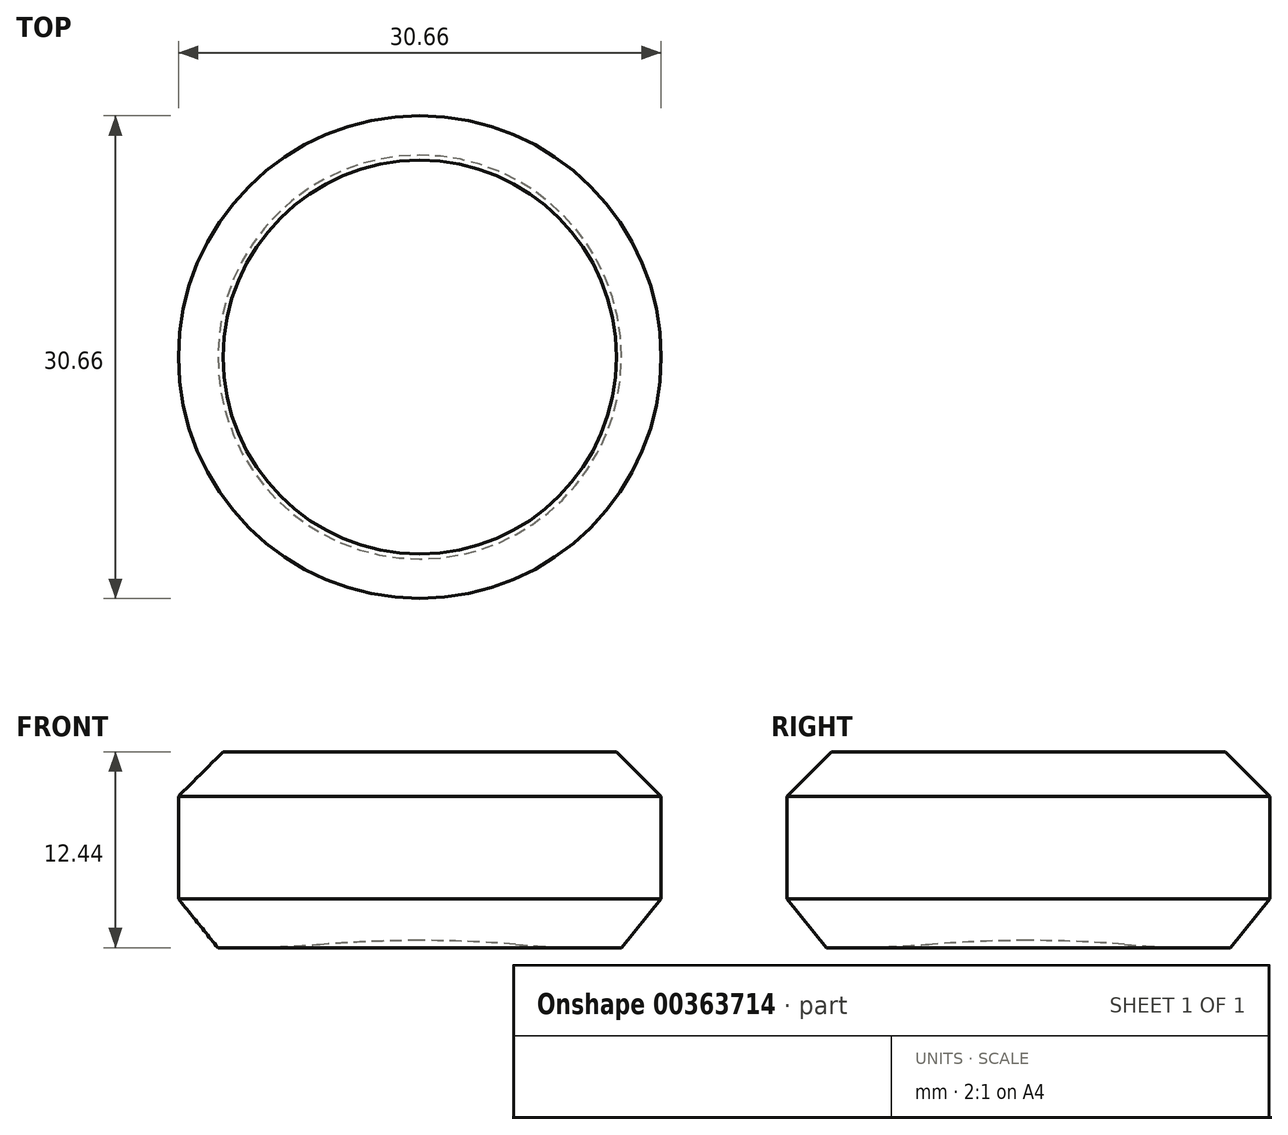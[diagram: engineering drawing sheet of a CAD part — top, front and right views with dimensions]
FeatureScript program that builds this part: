
annotation { "Feature Type Name" : "Feature", "Feature Type Description" : "" }
export const myFeature = defineFeature(function(context is Context, id is Id, definition is map)
    precondition{}
    {
        {
            var Q0;
            Q0=qCreatedBy(makeId("Front.planeOp"),FACE);
            var sketch = newSketch(context, id + "F0", { "sketchPlane" : qUnion([Q0])});
            skLineSegment(sketch, "E0", {"start": v(-6.5, 12.44) * mm, "end": v(-12.5, 12.44) * mm});
            skLineSegment(sketch, "E1", {"start": v(-12.5, 12.44) * mm, "end": v(-15.33, 9.61) * mm});
            skLineSegment(sketch, "E2", {"start": v(-15.33, 9.61) * mm, "end": v(-15.33, 3.11) * mm});
            skLineSegment(sketch, "E3", {"start": v(-15.33, 3.11) * mm, "end": v(-12.82, 0) * mm});
            skLineSegment(sketch, "E4", {"start": v(-12.82, 0) * mm, "end": v(-8.32, 0) * mm});
            skLineSegment(sketch, "E5", {"start": v(0, 0.46) * mm, "end": v(0, 12.44) * mm});
            skArc(sketch, "E6", {"start": v(0, 0.46) * mm, "mid": v(-4.17, 0.34) * mm, "end": v(-8.32, 0) * mm});
            skPoint(sketch, "E7.orphan", {"position": v(0, 0) * mm});
            skLineSegment(sketch, "E8", {"start": v(-6.5, 12.44) * mm, "end": v(0, 12.44) * mm});
            skSolve(sketch);
        }
        {
            var Q0;
            Q0=makeQuery(id+"F0.imprint","IMPRINT",FACE,{"disambiguationData":[TD([[makeQuery(id+"F0.imprint","IMPRINT",EDGE,{"derivedFrom":sQuery(id+"F0.wireOp",EDGE,"E0")}),1.0]])]});
            var Q1;
            Q1=sQuery(id+"F0.wireOp",EDGE,"E5");
            revolve(context, id + "F1", {"entities" : qUnion([Q0]), "axis" : qUnion([Q1]), "revolveType" : RevolveType.FULL});
        }
        {
            var Q0;
            Q0=makeQuery(id+"F1.opRevolve","SWEPT_EDGE",EDGE,{"disambiguationData":[OSD([sQuery(id+"F0.wireOp",EDGE,"E4"),sQuery(id+"F0.wireOp",EDGE,"E6")])]});
            fillet(context, id + "F2", {"entities" : qUnion([Q0]), "radius" : 65.54 * mm, "tangentPropagation" : true, "allowEdgeOverflow" : false});
        }
    });
